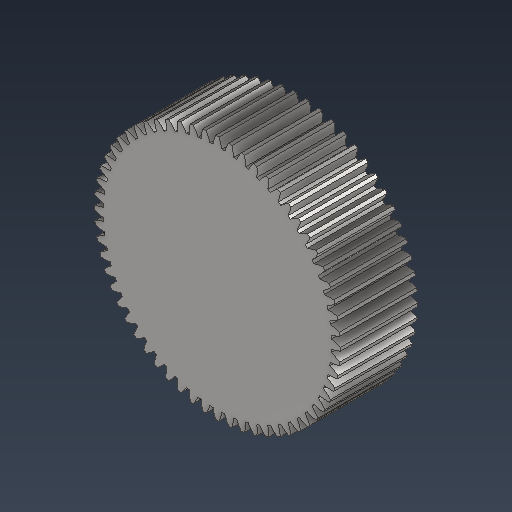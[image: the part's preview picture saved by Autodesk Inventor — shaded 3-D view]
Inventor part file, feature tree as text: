
AUTODESK INVENTOR PART (.ipt)
format: ipt  version: 2021 (Build 250183000, 183)  size: 415,744 bytes
history: native  units: mm (DEFAULTED — no unit token found)
features: plane x3, other x3, sketch x2, extrude x1
ambient origin geometry x8: Origin, YZ Plane, XZ Plane, XY Plane, X Axis, Y Axis, Z Axis, Center Point
bodies: Solid1 (feature_tree)
feature tree (9):
  extrude  "Extrusion1"  Depth=1.75mm TaperAngle=0.0deg
  plane  "Work Plane2"
  plane  "Work Plane8"
  plane  "Work Plane9"
  other  "Engrenagem reta"
  sketch  "Sketch1"  dims[d0=5.575177mm d1=1.75mm d2=0.0mm]
  sketch  "Sketch2"  dims[d3=5.4mm d4=10.0mm d5=0.0mm d16=3.597588mm d17=0.0mm d34=0.523599mm d39=0.0mm d41=0.0mm d43=3.597588mm d46=3.597588mm d47=0.0mm d48=0.0mm]
  other  "Srf1"
  other  "Diâmetro do flanco"
